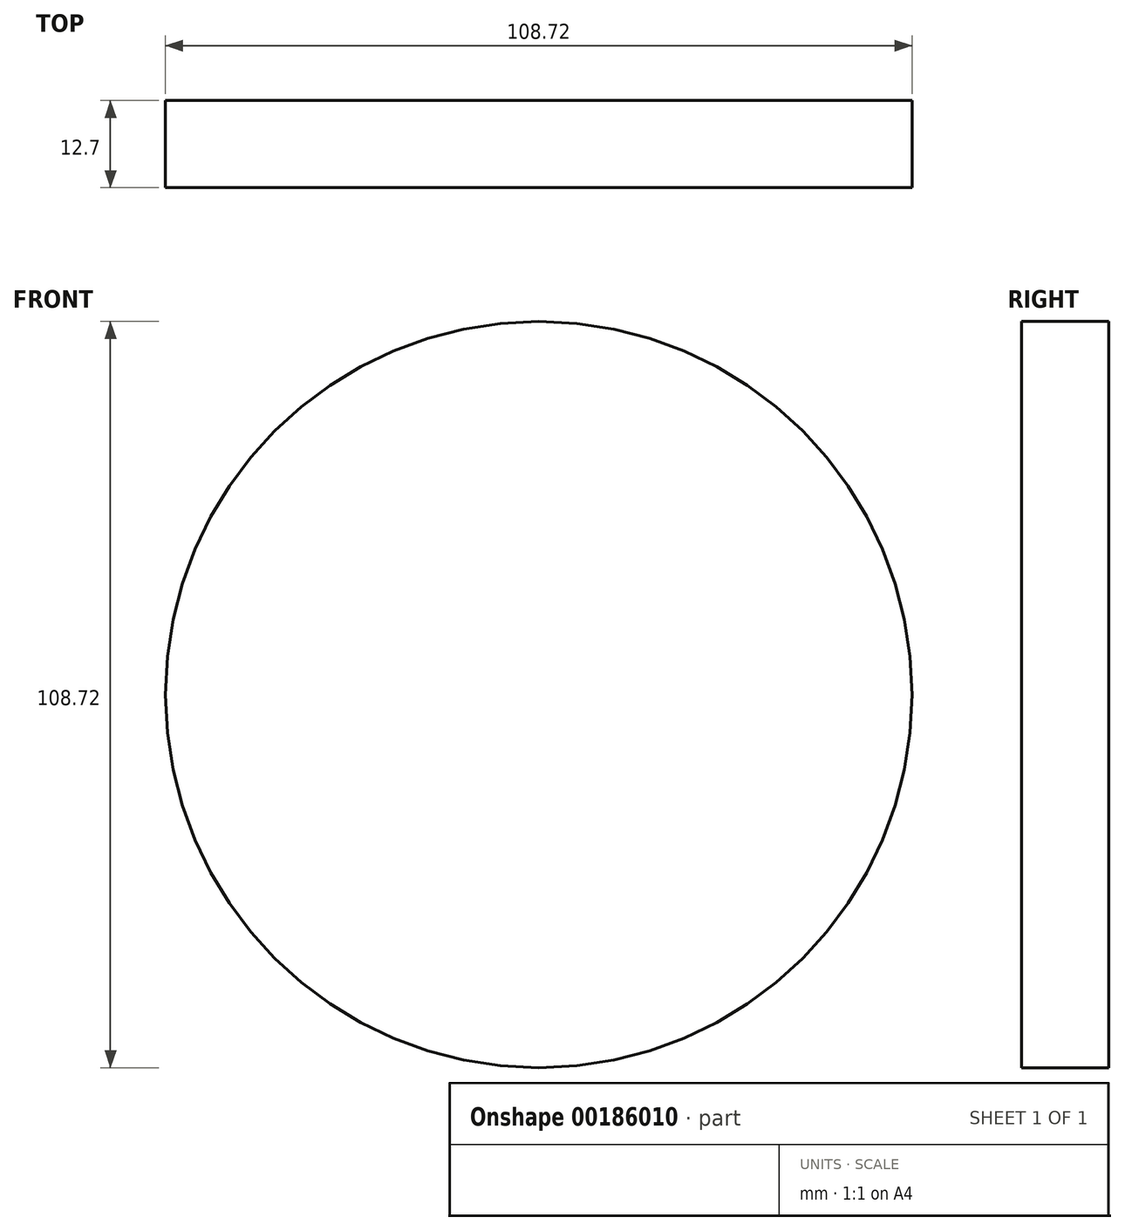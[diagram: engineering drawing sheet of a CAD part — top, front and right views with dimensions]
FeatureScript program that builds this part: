
annotation { "Feature Type Name" : "Feature", "Feature Type Description" : "" }
export const myFeature = defineFeature(function(context is Context, id is Id, definition is map)
    precondition{}
    {
        {
            var Q0;
            Q0=qCreatedBy(makeId("Front.planeOp"),FACE);
            var sketch = newSketch(context, id + "F0", { "sketchPlane" : qUnion([Q0])});
            skCircle(sketch, "E0", {"center": v(0, 0) * mm, "radius": 54.36 * mm});
            skSolve(sketch);
        }
        {
            var Q0;
            Q0=makeQuery(id+"F0.imprint","IMPRINT",FACE,{"disambiguationData":[TD([[makeQuery(id+"F0.imprint","IMPRINT",EDGE,{"derivedFrom":sQuery(id+"F0.wireOp",EDGE,"E0")}),1.0]])]});
            extrude(context, id + "F1", {"entities" : qUnion([Q0]), "depth" : 12.7 * mm});
        }
    });
